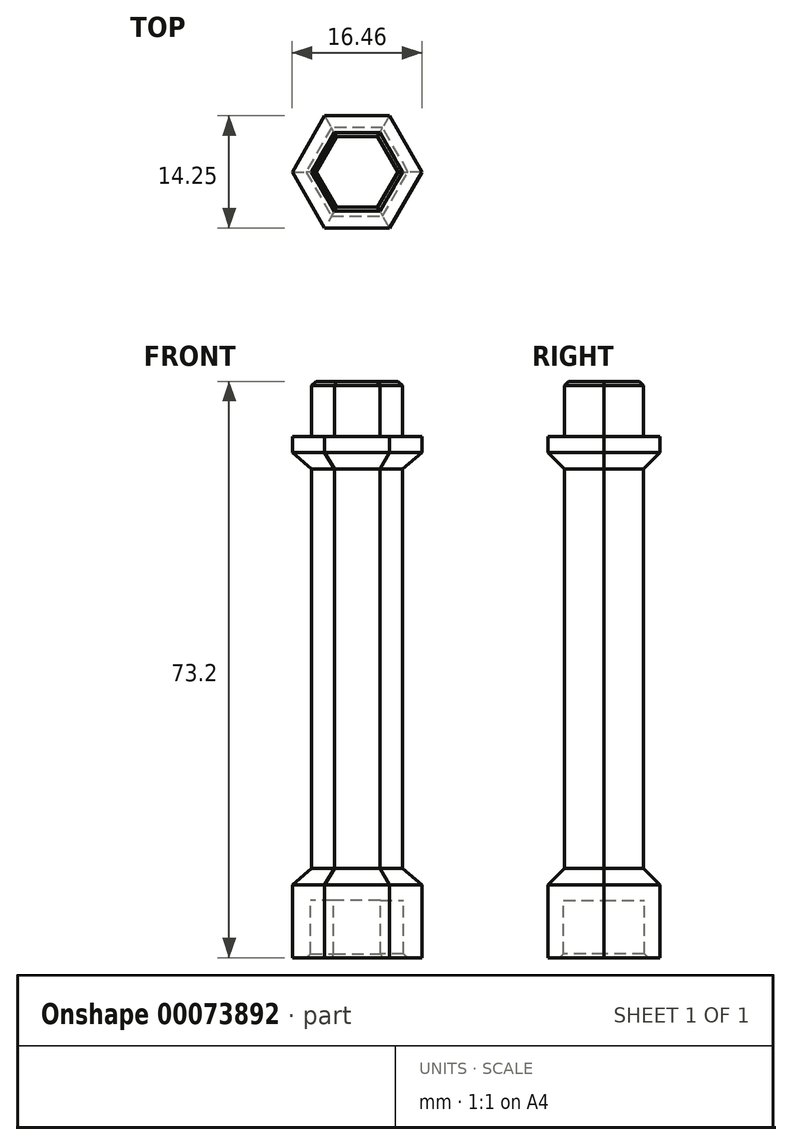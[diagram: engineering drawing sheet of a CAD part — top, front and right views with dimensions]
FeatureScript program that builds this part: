
annotation { "Feature Type Name" : "Feature", "Feature Type Description" : "" }
export const myFeature = defineFeature(function(context is Context, id is Id, definition is map)
    precondition{}
    {
        {
            var Q0;
            Q0=qCreatedBy(makeId("Top.planeOp"),FACE);
            var sketch = newSketch(context, id + "F0", { "sketchPlane" : qUnion([Q0])});
            skCircle(sketch, "E0.cCircle", {"center": v(0, 0) * mm, "radius": 5 * mm, "construction": true});
            skLineSegment(sketch, "E0.0", {"start": v(2.89, -5) * mm, "end": v(-2.89, -5) * mm});
            skLineSegment(sketch, "E0.1", {"start": v(-2.89, -5) * mm, "end": v(-5.77, 0) * mm});
            skLineSegment(sketch, "E0.2", {"start": v(-5.77, 0) * mm, "end": v(-2.89, 5) * mm});
            skLineSegment(sketch, "E0.3", {"start": v(-2.89, 5) * mm, "end": v(2.89, 5) * mm});
            skLineSegment(sketch, "E0.4", {"start": v(2.89, 5) * mm, "end": v(5.77, 0) * mm});
            skLineSegment(sketch, "E0.5", {"start": v(5.77, 0) * mm, "end": v(2.89, -5) * mm});
            skPoint(sketch, "E0.0.midPoint", {"position": v(0, -5) * mm});
            skSolve(sketch);
        }
        {
            var Q0;
            Q0=makeQuery(id+"F0.imprint","IMPRINT",FACE,{"disambiguationData":[TD([[makeQuery(id+"F0.imprint","IMPRINT",EDGE,{"derivedFrom":sQuery(id+"F0.wireOp",EDGE,"E0.0")}),-1.0]])]});
            extrude(context, id + "F1", {"entities" : qUnion([Q0]), "oppositeDirection" : true, "depth" : 76.2 * mm - 10 * mm - 7.25 * mm + 7 * mm});
        }
        {
            var Q0;
            Q0=makeQuery(id+"F1.opExtrude","CAP_FACE",FACE,{"disambiguationData":[OSD([sQuery(id+"F0.wireOp",EDGE,"E0.0"),sQuery(id+"F0.wireOp",EDGE,"E0.1"),sQuery(id+"F0.wireOp",EDGE,"E0.2"),sQuery(id+"F0.wireOp",EDGE,"E0.3"),sQuery(id+"F0.wireOp",EDGE,"E0.4"),sQuery(id+"F0.wireOp",EDGE,"E0.5")])],"isStart":false});
            var sketch = newSketch(context, id + "F2", { "sketchPlane" : qUnion([Q0])});
            skCircle(sketch, "E1.cCircle", {"center": v(0, 0) * mm, "radius": 5.12 * mm, "construction": true});
            skLineSegment(sketch, "E1.0", {"start": v(5.92, 0) * mm, "end": v(2.96, -5.13) * mm});
            skLineSegment(sketch, "E1.1", {"start": v(2.96, -5.12) * mm, "end": v(-2.96, -5.12) * mm});
            skLineSegment(sketch, "E1.2", {"start": v(-2.96, -5.12) * mm, "end": v(-5.92, 0) * mm});
            skLineSegment(sketch, "E1.3", {"start": v(-5.92, 0) * mm, "end": v(-2.96, 5.12) * mm});
            skLineSegment(sketch, "E1.4", {"start": v(-2.96, 5.12) * mm, "end": v(2.96, 5.12) * mm});
            skLineSegment(sketch, "E1.5", {"start": v(2.96, 5.12) * mm, "end": v(5.92, 0) * mm});
            skPoint(sketch, "E1.0.midPoint", {"position": v(4.44, -2.56) * mm});
            skLineSegment(sketch, "E2.0", {"start": v(-4.11, 7.12) * mm, "end": v(4.11, 7.12) * mm});
            skLineSegment(sketch, "E2.1", {"start": v(8.23, 0) * mm, "end": v(4.11, -7.13) * mm});
            skLineSegment(sketch, "E2.2", {"start": v(4.11, -7.12) * mm, "end": v(-4.11, -7.12) * mm});
            skLineSegment(sketch, "E2.3", {"start": v(4.11, 7.12) * mm, "end": v(8.23, 0) * mm});
            skLineSegment(sketch, "E2.4", {"start": v(-4.11, -7.13) * mm, "end": v(-8.23, 0) * mm});
            skLineSegment(sketch, "E2.5", {"start": v(-8.23, 0) * mm, "end": v(-4.11, 7.13) * mm});
            skSolve(sketch);
        }
        {
            var Q0;
            Q0=makeQuery(id+"F2.imprint","IMPRINT",FACE,{"disambiguationData":[TD([[makeQuery(id+"F2.imprint","IMPRINT",EDGE,{"derivedFrom":sQuery(id+"F2.wireOp",EDGE,"E1.0")}),1.0]])]});
            extrude(context, id + "F3", {"entities" : qUnion([Q0]), "depth" : 7.25 * mm});
        }
        {
            var Q0;
            Q0=makeQuery(id+"F3.opExtrude","CAP_FACE",FACE,{"disambiguationData":[OSD([sQuery(id+"F2.wireOp",EDGE,"E1.0"),sQuery(id+"F2.wireOp",EDGE,"E1.1"),sQuery(id+"F2.wireOp",EDGE,"E1.2"),sQuery(id+"F2.wireOp",EDGE,"E1.3"),sQuery(id+"F2.wireOp",EDGE,"E1.4"),sQuery(id+"F2.wireOp",EDGE,"E1.5"),sQuery(id+"F2.wireOp",EDGE,"E2.0"),sQuery(id+"F2.wireOp",EDGE,"E2.1"),sQuery(id+"F2.wireOp",EDGE,"E2.2"),sQuery(id+"F2.wireOp",EDGE,"E2.3"),sQuery(id+"F2.wireOp",EDGE,"E2.4"),sQuery(id+"F2.wireOp",EDGE,"E2.5")])],"isStart":true});
            var sketch = newSketch(context, id + "F4", { "sketchPlane" : qUnion([Q0])});
            skLineSegment(sketch, "E3.0", {"start": v(-4.11, -7.12) * mm, "end": v(4.11, -7.12) * mm});
            skLineSegment(sketch, "E3.1", {"start": v(4.11, -7.12) * mm, "end": v(8.23, 0) * mm});
            skLineSegment(sketch, "E3.2", {"start": v(8.23, 0) * mm, "end": v(4.11, 7.13) * mm});
            skLineSegment(sketch, "E3.3", {"start": v(4.11, 7.12) * mm, "end": v(-4.11, 7.12) * mm});
            skLineSegment(sketch, "E3.4", {"start": v(-8.23, 0) * mm, "end": v(-4.11, -7.13) * mm});
            skLineSegment(sketch, "E3.5", {"start": v(-4.11, 7.13) * mm, "end": v(-8.23, 0) * mm});
            skSolve(sketch);
        }
        {
            var Q0;
            Q0 = qSketchRegion(id + "F4", true);
            extrude(context, id + "F5", {"entities" : qUnion([Q0]), "operationType" : NewBodyOperationType.ADD, "depth" : 2 * mm});
        }
        {
            var Q0;
            Q0=makeQuery(id+"F1.opExtrude","CAP_FACE",FACE,{"disambiguationData":[OSD([sQuery(id+"F0.wireOp",EDGE,"E0.0"),sQuery(id+"F0.wireOp",EDGE,"E0.1"),sQuery(id+"F0.wireOp",EDGE,"E0.2"),sQuery(id+"F0.wireOp",EDGE,"E0.3"),sQuery(id+"F0.wireOp",EDGE,"E0.4"),sQuery(id+"F0.wireOp",EDGE,"E0.5")])],"isStart":true});
            cPlane(context, id + "F6", {"entities" : qUnion([Q0]), "cplaneType" : CPlaneType.OFFSET, "offset" : 7 * mm, "oppositeDirection" : true, "width" : 150 * mm, "height" : 150 * mm});
        }
        {
            var Q0;
            Q0=qCreatedBy(id+"F6.planeOp",FACE);
            var sketch = newSketch(context, id + "F7", { "sketchPlane" : qUnion([Q0])});
            skLineSegment(sketch, "E4.0", {"start": v(-4.11, -7.12) * mm, "end": v(4.11, -7.12) * mm});
            skLineSegment(sketch, "E4.1", {"start": v(4.11, -7.12) * mm, "end": v(8.23, 0) * mm});
            skLineSegment(sketch, "E4.2", {"start": v(8.23, 0) * mm, "end": v(4.11, 7.13) * mm});
            skLineSegment(sketch, "E4.3", {"start": v(4.11, 7.12) * mm, "end": v(-4.11, 7.12) * mm});
            skLineSegment(sketch, "E4.4", {"start": v(-8.23, 0) * mm, "end": v(-4.11, -7.13) * mm});
            skLineSegment(sketch, "E4.5", {"start": v(-4.11, 7.13) * mm, "end": v(-8.23, 0) * mm});
            skSolve(sketch);
        }
        {
            var Q0;
            Q0=makeQuery(id+"F7.imprint","IMPRINT",FACE,{"disambiguationData":[TD([[makeQuery(id+"F7.imprint","IMPRINT",EDGE,{"derivedFrom":sQuery(id+"F7.wireOp",EDGE,"E4.0")}),1.0]])]});
            extrude(context, id + "F8", {"entities" : qUnion([Q0]), "operationType" : NewBodyOperationType.ADD, "oppositeDirection" : true, "depth" : 2 * mm});
        }
        {
            var Q0;
            Q0=makeQuery(id+"F1.opExtrude","CAP_FACE",FACE,{"disambiguationData":[OSD([sQuery(id+"F0.wireOp",EDGE,"E0.0"),sQuery(id+"F0.wireOp",EDGE,"E0.1"),sQuery(id+"F0.wireOp",EDGE,"E0.2"),sQuery(id+"F0.wireOp",EDGE,"E0.3"),sQuery(id+"F0.wireOp",EDGE,"E0.4"),sQuery(id+"F0.wireOp",EDGE,"E0.5")])],"isStart":true});
            var Q1;
            Q1=makeQuery(id+"F3.opExtrude","CAP_EDGE",EDGE,{"disambiguationData":[OSD([sQuery(id+"F2.wireOp",EDGE,"E1.2")])],"isStart":false});
            var Q2;
            Q2=makeQuery(id+"F3.opExtrude","CAP_EDGE",EDGE,{"disambiguationData":[OSD([sQuery(id+"F2.wireOp",EDGE,"E1.3")])],"isStart":false});
            var Q3;
            Q3=makeQuery(id+"F3.opExtrude","CAP_EDGE",EDGE,{"disambiguationData":[OSD([sQuery(id+"F2.wireOp",EDGE,"E1.4")])],"isStart":false});
            var Q4;
            Q4=makeQuery(id+"F3.opExtrude","CAP_EDGE",EDGE,{"disambiguationData":[OSD([sQuery(id+"F2.wireOp",EDGE,"E1.5")])],"isStart":false});
            var Q5;
            Q5=makeQuery(id+"F3.opExtrude","CAP_EDGE",EDGE,{"disambiguationData":[OSD([sQuery(id+"F2.wireOp",EDGE,"E1.0")])],"isStart":false});
            var Q6;
            Q6=makeQuery(id+"F3.opExtrude","CAP_EDGE",EDGE,{"disambiguationData":[OSD([sQuery(id+"F2.wireOp",EDGE,"E1.1")])],"isStart":false});
            chamfer(context, id + "F9", {"entities" : qUnion([Q0, Q1, Q2, Q3, Q4, Q5, Q6]), "width" : .5 * mm, "tangentPropagation" : true});
        }
        {
            var Q0;
            Q0=makeQuery(id+"F5.boolean.opBoolean","INTERSECT",EDGE,{"derivedFrom":[makeQuery(id+"F1.opExtrude","SWEPT_FACE",FACE,{"disambiguationData":[OSD([sQuery(id+"F0.wireOp",EDGE,"E0.3")])]}),makeQuery(id+"F5.opExtrude","CAP_FACE",FACE,{"disambiguationData":[OSD([sQuery(id+"F4.wireOp",EDGE,"E3.0"),sQuery(id+"F4.wireOp",EDGE,"E3.1"),sQuery(id+"F4.wireOp",EDGE,"E3.2"),sQuery(id+"F4.wireOp",EDGE,"E3.3"),sQuery(id+"F4.wireOp",EDGE,"E3.4"),sQuery(id+"F4.wireOp",EDGE,"E3.5")])],"isStart":false})]});
            var Q1;
            Q1=makeQuery(id+"F5.boolean.opBoolean","INTERSECT",EDGE,{"derivedFrom":[makeQuery(id+"F1.opExtrude","SWEPT_FACE",FACE,{"disambiguationData":[OSD([sQuery(id+"F0.wireOp",EDGE,"E0.2")])]}),makeQuery(id+"F5.opExtrude","CAP_FACE",FACE,{"disambiguationData":[OSD([sQuery(id+"F4.wireOp",EDGE,"E3.0"),sQuery(id+"F4.wireOp",EDGE,"E3.1"),sQuery(id+"F4.wireOp",EDGE,"E3.2"),sQuery(id+"F4.wireOp",EDGE,"E3.3"),sQuery(id+"F4.wireOp",EDGE,"E3.4"),sQuery(id+"F4.wireOp",EDGE,"E3.5")])],"isStart":false})]});
            var Q2;
            Q2=makeQuery(id+"F5.boolean.opBoolean","INTERSECT",EDGE,{"derivedFrom":[makeQuery(id+"F1.opExtrude","SWEPT_FACE",FACE,{"disambiguationData":[OSD([sQuery(id+"F0.wireOp",EDGE,"E0.1")])]}),makeQuery(id+"F5.opExtrude","CAP_FACE",FACE,{"disambiguationData":[OSD([sQuery(id+"F4.wireOp",EDGE,"E3.0"),sQuery(id+"F4.wireOp",EDGE,"E3.1"),sQuery(id+"F4.wireOp",EDGE,"E3.2"),sQuery(id+"F4.wireOp",EDGE,"E3.3"),sQuery(id+"F4.wireOp",EDGE,"E3.4"),sQuery(id+"F4.wireOp",EDGE,"E3.5")])],"isStart":false})]});
            var Q3;
            Q3=makeQuery(id+"F5.boolean.opBoolean","INTERSECT",EDGE,{"derivedFrom":[makeQuery(id+"F1.opExtrude","SWEPT_FACE",FACE,{"disambiguationData":[OSD([sQuery(id+"F0.wireOp",EDGE,"E0.0")])]}),makeQuery(id+"F5.opExtrude","CAP_FACE",FACE,{"disambiguationData":[OSD([sQuery(id+"F4.wireOp",EDGE,"E3.0"),sQuery(id+"F4.wireOp",EDGE,"E3.1"),sQuery(id+"F4.wireOp",EDGE,"E3.2"),sQuery(id+"F4.wireOp",EDGE,"E3.3"),sQuery(id+"F4.wireOp",EDGE,"E3.4"),sQuery(id+"F4.wireOp",EDGE,"E3.5")])],"isStart":false})]});
            var Q4;
            Q4=makeQuery(id+"F5.boolean.opBoolean","INTERSECT",EDGE,{"derivedFrom":[makeQuery(id+"F1.opExtrude","SWEPT_FACE",FACE,{"disambiguationData":[OSD([sQuery(id+"F0.wireOp",EDGE,"E0.5")])]}),makeQuery(id+"F5.opExtrude","CAP_FACE",FACE,{"disambiguationData":[OSD([sQuery(id+"F4.wireOp",EDGE,"E3.0"),sQuery(id+"F4.wireOp",EDGE,"E3.1"),sQuery(id+"F4.wireOp",EDGE,"E3.2"),sQuery(id+"F4.wireOp",EDGE,"E3.3"),sQuery(id+"F4.wireOp",EDGE,"E3.4"),sQuery(id+"F4.wireOp",EDGE,"E3.5")])],"isStart":false})]});
            var Q5;
            Q5=makeQuery(id+"F5.boolean.opBoolean","INTERSECT",EDGE,{"derivedFrom":[makeQuery(id+"F1.opExtrude","SWEPT_FACE",FACE,{"disambiguationData":[OSD([sQuery(id+"F0.wireOp",EDGE,"E0.4")])]}),makeQuery(id+"F5.opExtrude","CAP_FACE",FACE,{"disambiguationData":[OSD([sQuery(id+"F4.wireOp",EDGE,"E3.0"),sQuery(id+"F4.wireOp",EDGE,"E3.1"),sQuery(id+"F4.wireOp",EDGE,"E3.2"),sQuery(id+"F4.wireOp",EDGE,"E3.3"),sQuery(id+"F4.wireOp",EDGE,"E3.4"),sQuery(id+"F4.wireOp",EDGE,"E3.5")])],"isStart":false})]});
            var Q6;
            Q6=makeQuery(id+"F8.boolean.opBoolean","INTERSECT",EDGE,{"derivedFrom":[makeQuery(id+"F1.opExtrude","SWEPT_FACE",FACE,{"disambiguationData":[OSD([sQuery(id+"F0.wireOp",EDGE,"E0.2")])]}),makeQuery(id+"F8.opExtrude","CAP_FACE",FACE,{"disambiguationData":[OSD([sQuery(id+"F7.wireOp",EDGE,"E4.0"),sQuery(id+"F7.wireOp",EDGE,"E4.1"),sQuery(id+"F7.wireOp",EDGE,"E4.2"),sQuery(id+"F7.wireOp",EDGE,"E4.3"),sQuery(id+"F7.wireOp",EDGE,"E4.4"),sQuery(id+"F7.wireOp",EDGE,"E4.5")])],"isStart":false})]});
            var Q7;
            Q7=makeQuery(id+"F8.boolean.opBoolean","INTERSECT",EDGE,{"derivedFrom":[makeQuery(id+"F1.opExtrude","SWEPT_FACE",FACE,{"disambiguationData":[OSD([sQuery(id+"F0.wireOp",EDGE,"E0.3")])]}),makeQuery(id+"F8.opExtrude","CAP_FACE",FACE,{"disambiguationData":[OSD([sQuery(id+"F7.wireOp",EDGE,"E4.0"),sQuery(id+"F7.wireOp",EDGE,"E4.1"),sQuery(id+"F7.wireOp",EDGE,"E4.2"),sQuery(id+"F7.wireOp",EDGE,"E4.3"),sQuery(id+"F7.wireOp",EDGE,"E4.4"),sQuery(id+"F7.wireOp",EDGE,"E4.5")])],"isStart":false})]});
            var Q8;
            Q8=makeQuery(id+"F8.boolean.opBoolean","INTERSECT",EDGE,{"derivedFrom":[makeQuery(id+"F1.opExtrude","SWEPT_FACE",FACE,{"disambiguationData":[OSD([sQuery(id+"F0.wireOp",EDGE,"E0.1")])]}),makeQuery(id+"F8.opExtrude","CAP_FACE",FACE,{"disambiguationData":[OSD([sQuery(id+"F7.wireOp",EDGE,"E4.0"),sQuery(id+"F7.wireOp",EDGE,"E4.1"),sQuery(id+"F7.wireOp",EDGE,"E4.2"),sQuery(id+"F7.wireOp",EDGE,"E4.3"),sQuery(id+"F7.wireOp",EDGE,"E4.4"),sQuery(id+"F7.wireOp",EDGE,"E4.5")])],"isStart":false})]});
            var Q9;
            Q9=makeQuery(id+"F8.boolean.opBoolean","INTERSECT",EDGE,{"derivedFrom":[makeQuery(id+"F1.opExtrude","SWEPT_FACE",FACE,{"disambiguationData":[OSD([sQuery(id+"F0.wireOp",EDGE,"E0.0")])]}),makeQuery(id+"F8.opExtrude","CAP_FACE",FACE,{"disambiguationData":[OSD([sQuery(id+"F7.wireOp",EDGE,"E4.0"),sQuery(id+"F7.wireOp",EDGE,"E4.1"),sQuery(id+"F7.wireOp",EDGE,"E4.2"),sQuery(id+"F7.wireOp",EDGE,"E4.3"),sQuery(id+"F7.wireOp",EDGE,"E4.4"),sQuery(id+"F7.wireOp",EDGE,"E4.5")])],"isStart":false})]});
            var Q10;
            Q10=makeQuery(id+"F8.boolean.opBoolean","INTERSECT",EDGE,{"derivedFrom":[makeQuery(id+"F1.opExtrude","SWEPT_FACE",FACE,{"disambiguationData":[OSD([sQuery(id+"F0.wireOp",EDGE,"E0.5")])]}),makeQuery(id+"F8.opExtrude","CAP_FACE",FACE,{"disambiguationData":[OSD([sQuery(id+"F7.wireOp",EDGE,"E4.0"),sQuery(id+"F7.wireOp",EDGE,"E4.1"),sQuery(id+"F7.wireOp",EDGE,"E4.2"),sQuery(id+"F7.wireOp",EDGE,"E4.3"),sQuery(id+"F7.wireOp",EDGE,"E4.4"),sQuery(id+"F7.wireOp",EDGE,"E4.5")])],"isStart":false})]});
            var Q11;
            Q11=makeQuery(id+"F8.boolean.opBoolean","INTERSECT",EDGE,{"derivedFrom":[makeQuery(id+"F1.opExtrude","SWEPT_FACE",FACE,{"disambiguationData":[OSD([sQuery(id+"F0.wireOp",EDGE,"E0.4")])]}),makeQuery(id+"F8.opExtrude","CAP_FACE",FACE,{"disambiguationData":[OSD([sQuery(id+"F7.wireOp",EDGE,"E4.0"),sQuery(id+"F7.wireOp",EDGE,"E4.1"),sQuery(id+"F7.wireOp",EDGE,"E4.2"),sQuery(id+"F7.wireOp",EDGE,"E4.3"),sQuery(id+"F7.wireOp",EDGE,"E4.4"),sQuery(id+"F7.wireOp",EDGE,"E4.5")])],"isStart":false})]});
            chamfer(context, id + "F10", {"entities" : qUnion([Q0, Q1, Q2, Q3, Q4, Q5, Q6, Q7, Q8, Q9, Q10, Q11]), "width" : 2 * mm + (.25 * mm / 2), "tangentPropagation" : true});
        }
        {
            var Q0;
            Q0=qCreatedBy(makeId("Front.planeOp"),FACE);
            var sketch = newSketch(context, id + "F11", { "sketchPlane" : qUnion([Q0])});
            skLineSegment(sketch, "E5", {"start": v(0, 0) * mm, "end": v(0, -66.2) * mm, "construction": true});
            skSolve(sketch);
        }
    });
